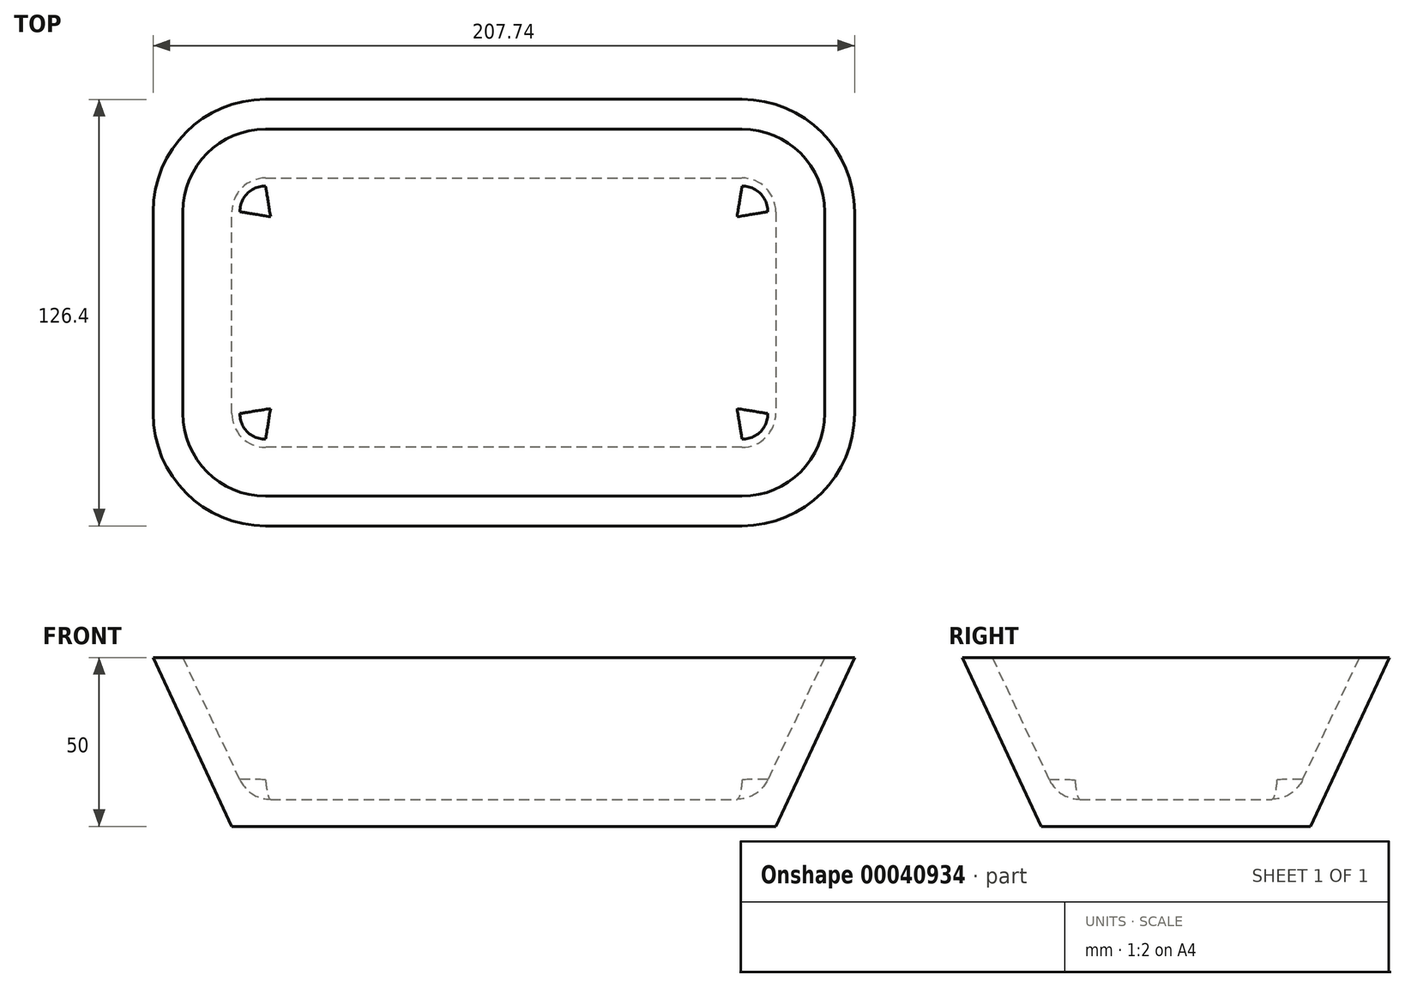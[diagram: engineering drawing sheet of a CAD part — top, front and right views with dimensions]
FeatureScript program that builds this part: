
annotation { "Feature Type Name" : "Feature", "Feature Type Description" : "" }
export const myFeature = defineFeature(function(context is Context, id is Id, definition is map)
    precondition{}
    {
        {
            var Q0;
            Q0=qCreatedBy(makeId("Top.planeOp"),FACE);
            var sketch = newSketch(context, id + "F0", { "sketchPlane" : qUnion([Q0])});
            skLineSegment(sketch, "E0.bottom", {"start": v(-68.28, 43.09) * mm, "end": v(72.83, 43.09) * mm});
            skLineSegment(sketch, "E0.top", {"start": v(-68.28, -36.68) * mm, "end": v(72.83, -36.68) * mm});
            skLineSegment(sketch, "E0.left", {"start": v(-78.28, 33.09) * mm, "end": v(-78.28, -26.68) * mm});
            skLineSegment(sketch, "E0.right", {"start": v(82.83, 33.09) * mm, "end": v(82.83, -26.68) * mm});
            skPoint(sketch, "E1.visualSharp", {"position": v(-78.28, 43.09) * mm});
            skArc(sketch, "E1.filletArc", {"start": v(-68.28, 43.09) * mm, "mid": v(-75.35, 40.16) * mm, "end": v(-78.28, 33.09) * mm});
            skPoint(sketch, "E2.visualSharp", {"position": v(-78.28, -36.68) * mm});
            skArc(sketch, "E2.filletArc", {"start": v(-78.28, -26.68) * mm, "mid": v(-75.35, -33.75) * mm, "end": v(-68.28, -36.68) * mm});
            skPoint(sketch, "E3.visualSharp", {"position": v(82.83, -36.68) * mm});
            skArc(sketch, "E3.filletArc", {"start": v(72.83, -36.68) * mm, "mid": v(79.9, -33.75) * mm, "end": v(82.83, -26.68) * mm});
            skPoint(sketch, "E4.visualSharp", {"position": v(82.83, 43.09) * mm});
            skArc(sketch, "E4.filletArc", {"start": v(82.83, 33.09) * mm, "mid": v(79.9, 40.16) * mm, "end": v(72.83, 43.09) * mm});
            skSolve(sketch);
        }
        {
            var Q0;
            Q0=makeQuery(id+"F0.imprint","IMPRINT",FACE,{"disambiguationData":[TD([[makeQuery(id+"F0.imprint","IMPRINT",EDGE,{"derivedFrom":sQuery(id+"F0.wireOp",EDGE,"E0.bottom")}),-1.0]])]});
            extrude(context, id + "F1", {"entities" : qUnion([Q0]), "depth" : 50 * mm, "hasDraft" : true, "draftAngle" : 25 * degree});
        }
        {
            var Q0;
            Q0=makeQuery(id+"F1.opExtrude","CAP_FACE",FACE,{"disambiguationData":[OSD([sQuery(id+"F0.wireOp",EDGE,"E0.bottom"),sQuery(id+"F0.wireOp",EDGE,"E0.top"),sQuery(id+"F0.wireOp",EDGE,"E0.left"),sQuery(id+"F0.wireOp",EDGE,"E0.right"),sQuery(id+"F0.wireOp",EDGE,"E1.filletArc"),sQuery(id+"F0.wireOp",EDGE,"E2.filletArc"),sQuery(id+"F0.wireOp",EDGE,"E3.filletArc"),sQuery(id+"F0.wireOp",EDGE,"E4.filletArc")])],"isStart":false});
            var Q1;
            Q1=makeQuery(id+"F1.opExtrude","SWEPT_BODY",BODY,{"disambiguationData":[OSD([sQuery(id+"F0.wireOp",EDGE,"E0.bottom"),sQuery(id+"F0.wireOp",EDGE,"E0.top"),sQuery(id+"F0.wireOp",EDGE,"E0.left"),sQuery(id+"F0.wireOp",EDGE,"E0.right"),sQuery(id+"F0.wireOp",EDGE,"E1.filletArc"),sQuery(id+"F0.wireOp",EDGE,"E2.filletArc"),sQuery(id+"F0.wireOp",EDGE,"E3.filletArc"),sQuery(id+"F0.wireOp",EDGE,"E4.filletArc")])]});
            shell(context, id + "F2", {"entities" : qUnion([Q0]), "parts" : qUnion([Q1]), "thickness" : 8 * mm});
        }
        {
            var Q0;
            Q0=makeQuery(id+"F2.opShell","OFFSET_FACE",FACE,{"disambiguationData":[OSD([sQuery(id+"F0.wireOp",EDGE,"E0.bottom"),sQuery(id+"F0.wireOp",EDGE,"E0.top"),sQuery(id+"F0.wireOp",EDGE,"E0.left"),sQuery(id+"F0.wireOp",EDGE,"E0.right"),sQuery(id+"F0.wireOp",EDGE,"E1.filletArc"),sQuery(id+"F0.wireOp",EDGE,"E2.filletArc"),sQuery(id+"F0.wireOp",EDGE,"E3.filletArc"),sQuery(id+"F0.wireOp",EDGE,"E4.filletArc")])]});
            fillet(context, id + "F3", {"entities" : qUnion([Q0]), "radius" : 10 * mm, "tangentPropagation" : true, "allowEdgeOverflow" : false});
        }
    });
